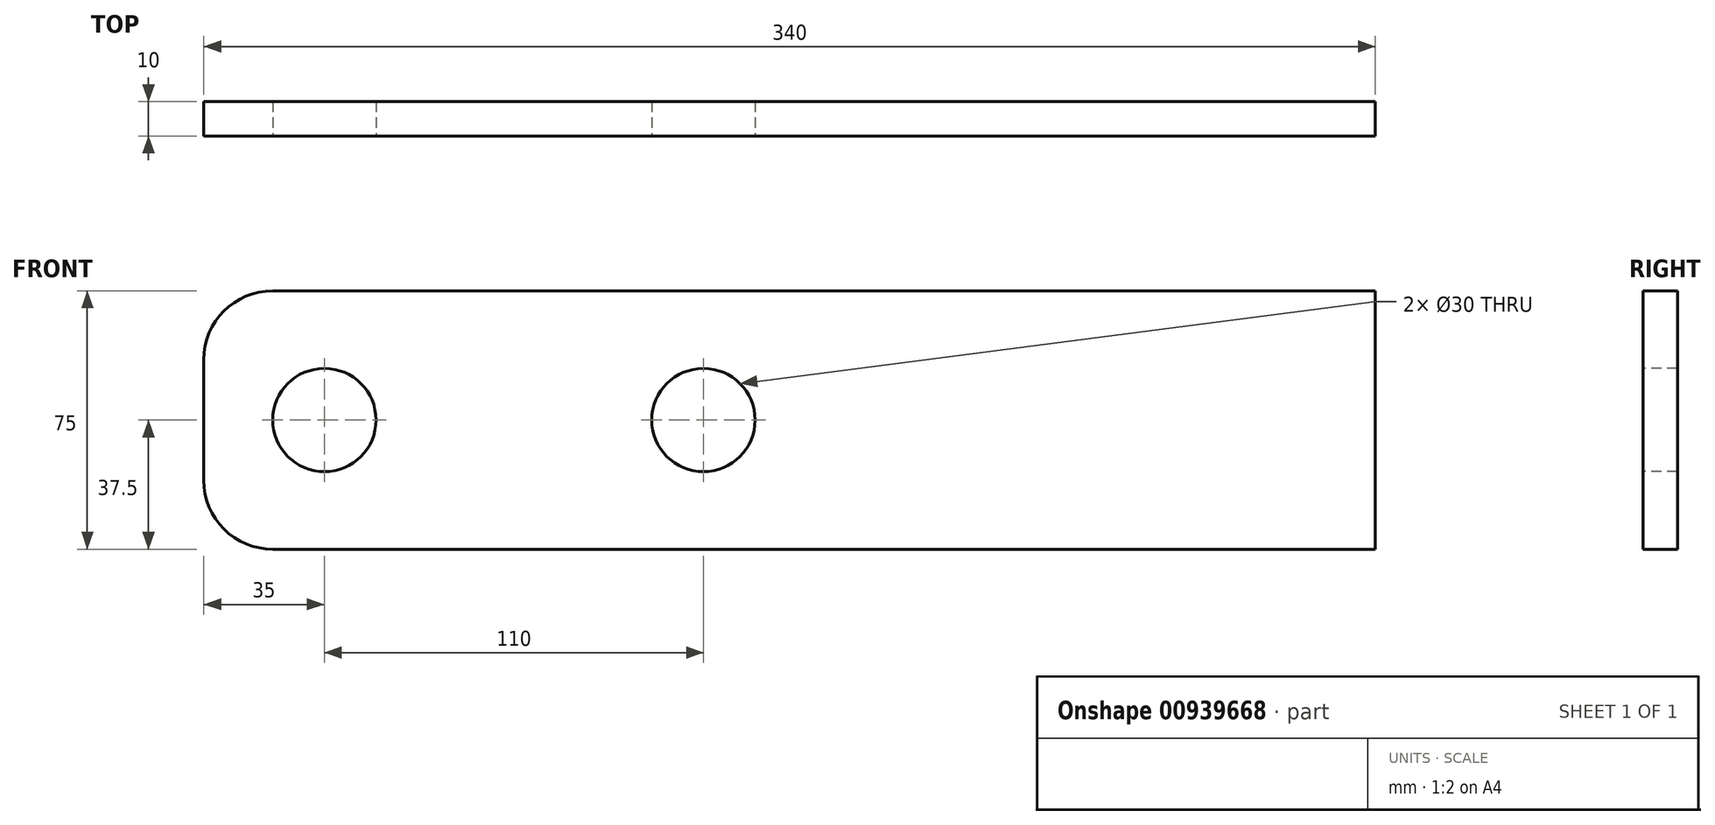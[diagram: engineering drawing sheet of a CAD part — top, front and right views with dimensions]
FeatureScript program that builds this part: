
annotation { "Feature Type Name" : "Feature", "Feature Type Description" : "" }
export const myFeature = defineFeature(function(context is Context, id is Id, definition is map)
    precondition{}
    {
        {
            var Q0;
            Q0=qCreatedBy(makeId("Front.planeOp"),FACE);
            var sketch = newSketch(context, id + "F0", { "sketchPlane" : qUnion([Q0])});
            skLineSegment(sketch, "E0.bottom", {"start": v(170, -37.5) * mm, "end": v(-170, -37.5) * mm});
            skLineSegment(sketch, "E0.top", {"start": v(170, 37.5) * mm, "end": v(-170, 37.5) * mm});
            skLineSegment(sketch, "E0.left", {"start": v(170, -37.5) * mm, "end": v(170, 37.5) * mm});
            skLineSegment(sketch, "E0.right", {"start": v(-170, -37.5) * mm, "end": v(-170, 37.5) * mm});
            skPoint(sketch, "E0.middle", {"position": v(0, 0) * mm});
            skSolve(sketch);
        }
        {
            var Q0;
            Q0 = qSketchRegion(id + "F0", true);
            extrude(context, id + "F1", {"entities" : qUnion([Q0]), "depth" : 10 * mm, "offsetDistance" : 25 * mm});
        }
        {
            var Q0;
            Q0=makeQuery(id+"F1.opExtrude","SWEPT_EDGE",EDGE,{"disambiguationData":[OSD([sQuery(id+"F0.wireOp",EDGE,"E0.top"),sQuery(id+"F0.wireOp",EDGE,"E0.right")])]});
            var Q1;
            Q1=makeQuery(id+"F1.opExtrude","SWEPT_EDGE",EDGE,{"disambiguationData":[OSD([sQuery(id+"F0.wireOp",EDGE,"E0.bottom"),sQuery(id+"F0.wireOp",EDGE,"E0.right")])]});
            fillet(context, id + "F2", {"entities" : qUnion([Q0, Q1]), "radius" : 20 * mm, "tangentPropagation" : true, "allowEdgeOverflow" : false});
        }
        {
            var Q0;
            Q0=qCreatedBy(makeId("Front.planeOp"),FACE);
            var sketch = newSketch(context, id + "F3", { "sketchPlane" : qUnion([Q0])});
            skCircle(sketch, "E1", {"center": v(-135, 0) * mm, "radius": 15 * mm});
            skCircle(sketch, "E2", {"center": v(-25, 0) * mm, "radius": 15 * mm});
            skSolve(sketch);
        }
        {
            var Q0;
            Q0 = qSketchRegion(id + "F3", true);
            extrude(context, id + "F4", {"entities" : qUnion([Q0]), "operationType" : NewBodyOperationType.REMOVE, "endBound" : BoundingType.THROUGH_ALL, "oppositeDirection" : true, "depth" : 25 * mm, "offsetDistance" : 25 * mm, "hasSecondDirection" : true, "secondDirectionOppositeDirection" : false, "secondDirectionDepth" : 25 * mm});
        }
    });
